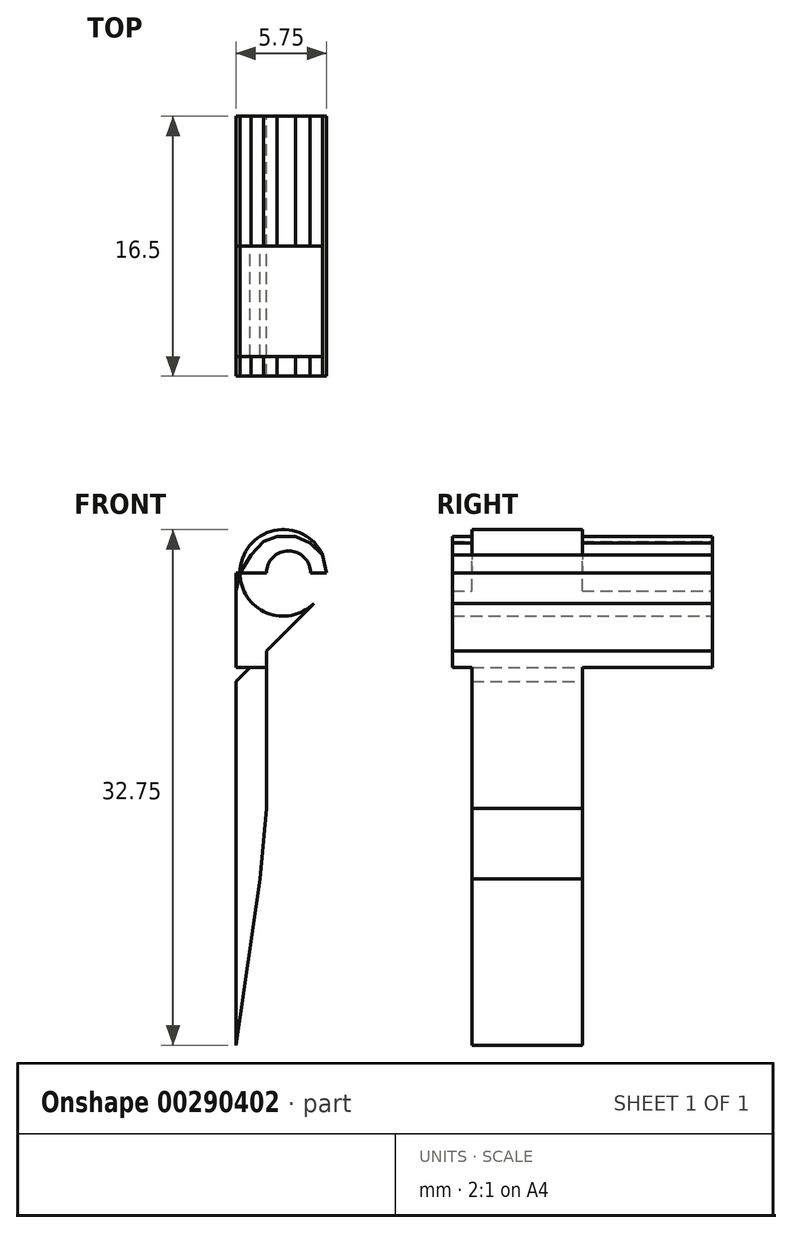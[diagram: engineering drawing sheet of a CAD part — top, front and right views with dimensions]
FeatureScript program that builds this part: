
annotation { "Feature Type Name" : "Feature", "Feature Type Description" : "" }
export const myFeature = defineFeature(function(context is Context, id is Id, definition is map)
    precondition{}
    {
        {
            var Q0;
            Q0=qCreatedBy(makeId("Front.planeOp"),FACE);
            var sketch = newSketch(context, id + "F0", { "sketchPlane" : qUnion([Q0])});
            skLineSegment(sketch, "E0", {"start": v(0, -30) * mm, "end": v(0, 0) * mm});
            skLineSegment(sketch, "E1", {"start": v(0, 0) * mm, "end": v(-6, 0) * mm});
            skLineSegment(sketch, "E2", {"start": v(0.75, -30) * mm, "end": v(34.75, -30) * mm, "construction": true});
            skLineSegment(sketch, "E3", {"start": v(34, -30) * mm, "end": v(34, 6.03) * mm, "construction": true});
            skCircle(sketch, "E4", {"center": v(-2.66, 0) * mm, "radius": 1.8 * mm, "construction": true});
            skCircle(sketch, "E5", {"center": v(-2.66, 0) * mm, "radius": 1.4 * mm});
            skPoint(sketch, "E6", {"position": v(-4.46, 0) * mm});
            skPoint(sketch, "E7", {"position": v(-5.35, 0) * mm});
            skPoint(sketch, "E8", {"position": v(-4.06, 0) * mm});
            skCircle(sketch, "E9", {"center": v(-3, 0) * mm, "radius": 2.75 * mm});
            skLineSegment(sketch, "E10", {"start": v(-1.05, -1.94) * mm, "end": v(-6, -6.88) * mm});
            skLineSegment(sketch, "E11", {"start": v(-4.06, -14.95) * mm, "end": v(-4.46, -19.43) * mm, "construction": true});
            skLineSegment(sketch, "E12", {"start": v(-4.46, -19.43) * mm, "end": v(-6, -30) * mm});
            skLineSegment(sketch, "E13", {"start": v(-5.75, 0) * mm, "end": v(-5.05, 1.14) * mm});
            skLineSegment(sketch, "E14", {"start": v(-5.05, 1.14) * mm, "end": v(-4.25, 1.99) * mm});
            skLineSegment(sketch, "E15", {"start": v(-4.25, 1.99) * mm, "end": v(-3.38, 2.32) * mm});
            skLineSegment(sketch, "E16", {"start": v(-3.38, 2.32) * mm, "end": v(-2.23, 2.32) * mm});
            skLineSegment(sketch, "E17", {"start": v(-2.23, 2.32) * mm, "end": v(-1.28, 1.91) * mm});
            skLineSegment(sketch, "E18", {"start": v(-1.28, 1.91) * mm, "end": v(-0.5, 1.14) * mm});
            skLineSegment(sketch, "E19", {"start": v(-0.5, 1.14) * mm, "end": v(-0.25, 0) * mm});
            skLineSegment(sketch, "E20", {"start": v(-5.25, -30) * mm, "end": v(-3.15, -30) * mm});
            skLineSegment(sketch, "E21", {"start": v(-4.06, -8.65) * mm, "end": v(-4.06, -14.95) * mm});
            skLineSegment(sketch, "E22", {"start": v(-4.06, -14.95) * mm, "end": v(-4.46, -19.43) * mm});
            skLineSegment(sketch, "E23", {"start": v(-6, -30) * mm, "end": v(-6, -4.8) * mm});
            skLineSegment(sketch, "E24", {"start": v(-6.2, -2.02) * mm, "end": v(-5.75, 0) * mm});
            skLineSegment(sketch, "E25", {"start": v(-4.06, -8.65) * mm, "end": v(-6, -8.65) * mm});
            skLineSegment(sketch, "E26", {"start": v(-2.66, 0) * mm, "end": v(-6, 0) * mm});
            skLineSegment(sketch, "E27", {"start": v(-6, 0) * mm, "end": v(-6, -6) * mm});
            skLineSegment(sketch, "E28", {"start": v(-6, -6) * mm, "end": v(-6, -8.65) * mm});
            skLineSegment(sketch, "E29", {"start": v(-6, -6) * mm, "end": v(-4.06, -6) * mm});
            skLineSegment(sketch, "E30", {"start": v(-4.06, -8.65) * mm, "end": v(-4.06, -6) * mm});
            skLineSegment(sketch, "E31", {"start": v(-4.06, -6) * mm, "end": v(-4.06, -4.95) * mm});
            skPoint(sketch, "E32", {"position": v(-1.26, 0) * mm});
            skSolve(sketch);
        }
        {
            var Q0;
            {var subQ0=sQuery(id+"F0.wireOp",EDGE,"pF8hiRyQ-AT2O-Hw3t-gXbs-V2D3RN1RvF7Z");var subQ3=sQuery(id+"F0.wireOp",EDGE,"nOz5UhaC-nWL8-Xr70-sTCd-52PdFmUEBBvD");var subQ5=makeQuery(id+"F0.imprint","INTERSECT",VERTEX,{"derivedFrom":[subQ0,subQ3]});Q0=makeQuery(id+"F0.imprint","IMPRINT",FACE,{"disambiguationData":[TD([[makeQuery(id+"F0.imprint","IMPRINT",EDGE,{"disambiguationData":[TD([[subQ5,-1.0]])],"derivedFrom":subQ3}),-1.0]])]});}
            var Q1;
            Q1=makeQuery(id+"F0.imprint","IMPRINT",FACE,{"disambiguationData":[TD([[makeQuery(id+"F0.imprint","IMPRINT",EDGE,{"derivedFrom":sQuery(id+"F0.wireOp",EDGE,"Dvm8OXYp-memO-CaQP-tHji-m7OZ0B7q4PlM")}),1.0]])]});
            var Q2;
            {var subQ3=sQuery(id+"F0.wireOp",EDGE,"t8jRmxTm-ZC1a-fYBk-IYAb-11mtiPYUYwxX");Q2=makeQuery(id+"F0.imprint","IMPRINT",FACE,{"disambiguationData":[TD([[makeQuery(id+"F0.imprint","IMPRINT",EDGE,{"derivedFrom":subQ3}),-1.0]])]});}
            var Q3;
            {var subQ0=sQuery(id+"F0.wireOp",EDGE,"E13");Q3=makeQuery(id+"F0.imprint","IMPRINT",FACE,{"disambiguationData":[TD([[makeQuery(id+"F0.imprint","IMPRINT",EDGE,{"derivedFrom":subQ0}),-1.0]])]});}
            var Q4;
            {var subQ2=sQuery(id+"F0.wireOp",EDGE,"E1");var subQ4=sQuery(id+"F0.wireOp",EDGE,"E5");var subQ6=makeQuery(id+"F0.imprint","INTERSECT",VERTEX,{"disambiguationData":[OD(0.0)],"derivedFrom":[subQ2,subQ4]});Q4=makeQuery(id+"F0.imprint","IMPRINT",FACE,{"disambiguationData":[TD([[makeQuery(id+"F0.imprint","IMPRINT",EDGE,{"disambiguationData":[TD([[subQ6,1.0]])],"derivedFrom":subQ4}),-1.0]])]});}
            var Q5;
            {var subQ7=sQuery(id+"F0.wireOp",EDGE,"21qWk6PW-NGkE-VNRS-IPtG-xVmnf3USF49F");Q5=makeQuery(id+"F0.imprint","IMPRINT",FACE,{"disambiguationData":[TD([[makeQuery(id+"F0.imprint","IMPRINT",EDGE,{"derivedFrom":subQ7}),-1.0]])]});}
            var Q6;
            {var subQ1=sQuery(id+"F0.wireOp",EDGE,"E9");var subQ5=sQuery(id+"F0.wireOp",EDGE,"E10");var subQ10=makeQuery(id+"F0.imprint","INTERSECT",VERTEX,{"derivedFrom":[subQ1,subQ5]});Q6=makeQuery(id+"F0.imprint","IMPRINT",FACE,{"disambiguationData":[TD([[makeQuery(id+"F0.imprint","IMPRINT",EDGE,{"disambiguationData":[TD([[subQ10,-1.0]])],"derivedFrom":subQ5}),-1.0]])]});}
            var Q7;
            {var subQ0=sQuery(id+"F0.wireOp",EDGE,"E31");Q7=makeQuery(id+"F0.imprint","IMPRINT",FACE,{"disambiguationData":[TD([[makeQuery(id+"F0.imprint","IMPRINT",EDGE,{"derivedFrom":subQ0}),1.0]])]});}
            extrude(context, id + "F1", {"entities" : qUnion([Q0, Q1, Q2, Q3, Q4, Q5, Q6, Q7]), "endBound" : BoundingType.SYMMETRIC, "depth" : 16.5 * mm});
        }
        {
            var Q0;
            {var subQ0=sQuery(id+"F0.wireOp",EDGE,"E13");Q0=makeQuery(id+"F0.imprint","IMPRINT",FACE,{"disambiguationData":[TD([[makeQuery(id+"F0.imprint","IMPRINT",EDGE,{"derivedFrom":subQ0}),1.0]])]});}
            var Q1;
            {var subQ0=sQuery(id+"F0.wireOp",EDGE,"E26");var subQ3=sQuery(id+"F0.wireOp",EDGE,"E27");var subQ5=makeQuery(id+"F0.imprint","INTERSECT",VERTEX,{"derivedFrom":[subQ0,subQ3]});Q1=makeQuery(id+"F0.imprint","IMPRINT",FACE,{"disambiguationData":[TD([[makeQuery(id+"F0.imprint","IMPRINT",EDGE,{"disambiguationData":[TD([[subQ5,-1.0]])],"derivedFrom":subQ3}),1.0]])]});}
            var Q2;
            Q2=makeQuery(id+"F0.imprint","IMPRINT",FACE,{"disambiguationData":[TD([[makeQuery(id+"F0.imprint","IMPRINT",EDGE,{"derivedFrom":sQuery(id+"F0.wireOp",EDGE,"E12")}),-1.0]])]});
            var Q3;
            {var subQ6=sQuery(id+"F0.wireOp",EDGE,"E25");Q3=makeQuery(id+"F0.imprint","IMPRINT",FACE,{"disambiguationData":[TD([[makeQuery(id+"F0.imprint","IMPRINT",EDGE,{"derivedFrom":subQ6}),-1.0]])]});}
            var Q4;
            {var subQ0=sQuery(id+"F0.wireOp",EDGE,"E28");var subQ1=sQuery(id+"F0.wireOp",EDGE,"E10");var subQ2=makeQuery(id+"F0.imprint","INTERSECT",VERTEX,{"derivedFrom":[subQ1,subQ0]});Q4=makeQuery(id+"F0.imprint","IMPRINT",FACE,{"disambiguationData":[TD([[makeQuery(id+"F0.imprint","IMPRINT",EDGE,{"disambiguationData":[TD([[subQ2,1.0]])],"derivedFrom":subQ1}),-1.0]])]});}
            extrude(context, id + "F2", {"entities" : qUnion([Q0, Q1, Q2, Q3, Q4]), "operationType" : NewBodyOperationType.ADD, "depth" : 7 * mm});
        }
    });
